# Revit family: Gira_264003
name_source: partatom
category: Elektroinstallationen
revit_build: Autodesk Revit 2017 (Build: 20160225_1515(x64)
units: mm (PartAtom-declared; Revit-internal decimal feet)

## family parameters
Basisbauteil = Fläche
Beim Laden mit Abzugskörper schneiden = Nein
Bemaßung runder Anschluss = Durchmesser verwenden
Beschriftungsausrichtung beibehalten = Nein
Gemeinsam genutzt = Nein
Raumberechnungspunkt = Nein
Teiletyp = Normal

## types (1)
- Gira_264003
    Assembly arrangement = Central cover plate
    BIM = https://media.stage.bim.site und Tasten.rfa
    Bauelement = Sys55_Abdeckung_Schalten und Tasten
    Beschreibung = Cov.30° in.sp.sup.r.MJ 2g Sys55 PW,Cover plate with 30 angled socket outlet and inscription field for Modular Jack support ring,,pure white glossy,
    Colour = White
    Data sheet = https://katalog.gira.de
    GTIN = 4010337460138
    HAN = 264003
    Halogen free = Ja
    Hersteller = Gira
    Imprintable label = With indication plate
    Luster terminal = Nein
    Material = Plastic
    Material quality = Thermoplastic
    Mounting method = Other
    Productwebsite = http://katalog.gira.de
    RAL-number (akin) = 9010
    Suitable for degree of protection (IP) = IP20
    Support ring = Nein
    Surface finishing = Glossy
    Surface protection = Other
    Transparent = Nein
    Type of fastening = Other
    Typname = Cov. 30° + in.sp. f. sup.ring MJ 2-g System 55 p.white
    URL = https://www.gira.de
    Utilization = Modular Jack
    Vorgabe-Ansicht = 1219 mm
    With dust cover = Nein
    With hinged lid = Nein
    With imprint = Nein
    With strain relief = Nein

## geometry (parser evidence)
native form markers: Sweep x6
no freeform markers — native parametric forms only
